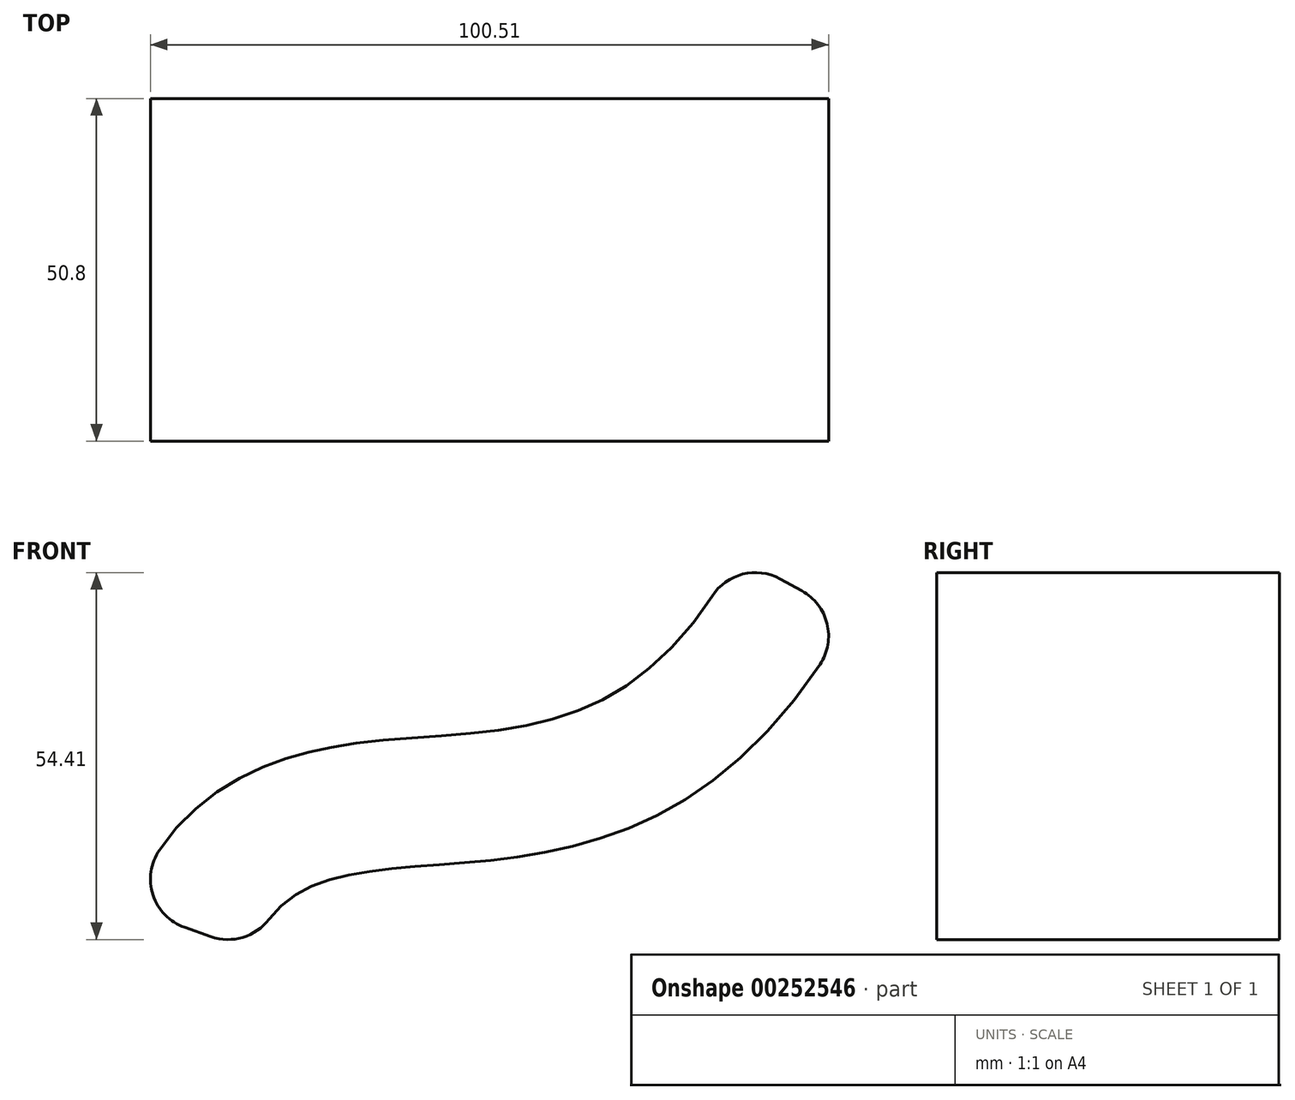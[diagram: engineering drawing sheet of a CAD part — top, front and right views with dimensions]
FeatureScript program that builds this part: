
annotation { "Feature Type Name" : "Feature", "Feature Type Description" : "" }
export const myFeature = defineFeature(function(context is Context, id is Id, definition is map)
    precondition{}
    {
        {
            var Q0;
            Q0=qCreatedBy(makeId("Front.planeOp"),FACE);
            var sketch = newSketch(context, id + "F0", { "sketchPlane" : qUnion([Q0])});
            skFitSpline(sketch, "E0", {"points": [v(-37.08, -13.7) * mm, v(51.34, 35.9) * mm], "startDerivative": vector(28.36, 80.65) * mm, "endDerivative": vector(93.6, 170.61) * mm});
            skFitSpline(sketch, "E1.0", {"points": [v(-55.05, -7.39) * mm, v(-54.5, -5.8) * mm, v(-53.18, -2.69) * mm, v(-50.53, 1.73) * mm, v(-47.25, 5.7) * mm, v(-43.5, 9.02) * mm, v(-39.53, 11.64) * mm, v(-35.54, 13.6) * mm, v(-31.66, 15) * mm, v(-27.96, 16) * mm, v(-24.43, 16.69) * mm, v(-19.94, 17.34) * mm, v(-14.66, 17.82) * mm, v(-8.72, 18.24) * mm, v(-3.12, 18.74) * mm, v(2.16, 19.48) * mm, v(7.1, 20.58) * mm, v(11.72, 22.14) * mm, v(16.16, 24.3) * mm, v(20.56, 27.26) * mm, v(25.1, 31.37) * mm, v(29.81, 37.05) * mm, v(33.04, 42.14) * mm, v(34.64, 45.07) * mm]});
            skLineSegment(sketch, "E2", {"start": v(-55.05, -7.39) * mm, "end": v(-37.08, -13.7) * mm});
            skLineSegment(sketch, "E3", {"start": v(34.64, 45.07) * mm, "end": v(51.34, 35.9) * mm});
            skSolve(sketch);
        }
        {
            var Q0;
            Q0=makeQuery(id+"F0.imprint","IMPRINT",FACE,{"disambiguationData":[TD([[makeQuery(id+"F0.imprint","IMPRINT",EDGE,{"derivedFrom":sQuery(id+"F0.wireOp",EDGE,"E0")}),1.0]])]});
            extrude(context, id + "F1", {"entities" : qUnion([Q0]), "depth" : 50.8 * mm});
        }
        {
            var Q0;
            Q0=makeQuery(id+"F1.opExtrude","SWEPT_EDGE",EDGE,{"disambiguationData":[OSD([sQuery(id+"F0.wireOp",EDGE,"E1.0"),sQuery(id+"F0.wireOp",EDGE,"E3")])]});
            var Q1;
            Q1=makeQuery(id+"F1.opExtrude","SWEPT_EDGE",EDGE,{"disambiguationData":[OSD([sQuery(id+"F0.wireOp",EDGE,"E0"),sQuery(id+"F0.wireOp",EDGE,"E3")])]});
            var Q2;
            Q2=makeQuery(id+"F1.opExtrude","SWEPT_EDGE",EDGE,{"disambiguationData":[OSD([sQuery(id+"F0.wireOp",EDGE,"E1.0"),sQuery(id+"F0.wireOp",EDGE,"E2")])]});
            var Q3;
            Q3=makeQuery(id+"F1.opExtrude","SWEPT_EDGE",EDGE,{"disambiguationData":[OSD([sQuery(id+"F0.wireOp",EDGE,"E0"),sQuery(id+"F0.wireOp",EDGE,"E2")])]});
            fillet(context, id + "F2", {"entities" : qUnion([Q0, Q1, Q2, Q3]), "radius" : 7.62 * mm, "tangentPropagation" : true, "allowEdgeOverflow" : false});
        }
    });
